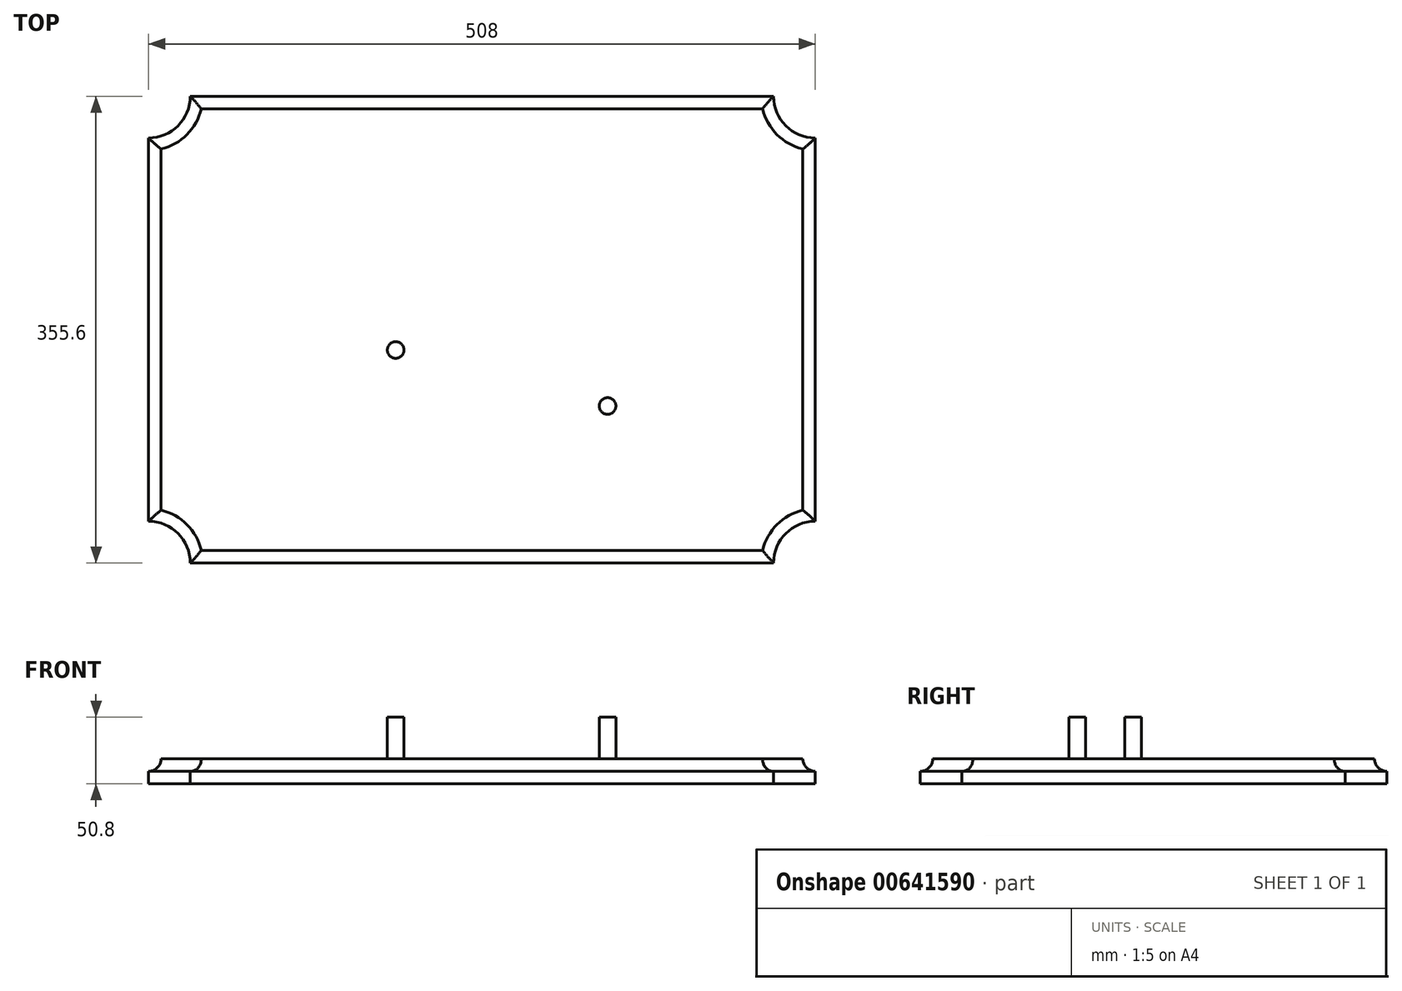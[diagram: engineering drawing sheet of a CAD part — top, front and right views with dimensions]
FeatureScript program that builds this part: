
annotation { "Feature Type Name" : "Feature", "Feature Type Description" : "" }
export const myFeature = defineFeature(function(context is Context, id is Id, definition is map)
    precondition{}
    {
        {
            var Q0;
            Q0=qCreatedBy(makeId("Top.planeOp"),FACE);
            var sketch = newSketch(context, id + "F0", { "sketchPlane" : qUnion([Q0])});
            skLineSegment(sketch, "E0.bottom", {"start": v(222.25, 177.8) * mm, "end": v(-222.25, 177.8) * mm});
            skLineSegment(sketch, "E0.top", {"start": v(222.25, -177.8) * mm, "end": v(-222.25, -177.8) * mm});
            skLineSegment(sketch, "E0.left", {"start": v(254, 146.05) * mm, "end": v(254, -146.05) * mm});
            skLineSegment(sketch, "E0.right", {"start": v(-254, 146.05) * mm, "end": v(-254, -146.05) * mm});
            skPoint(sketch, "E0.middle", {"position": v(0, 0) * mm});
            skArc(sketch, "E1", {"start": v(-254, 146.05) * mm, "mid": v(-231.55, 155.35) * mm, "end": v(-222.25, 177.8) * mm});
            skArc(sketch, "E2", {"start": v(-222.25, -177.8) * mm, "mid": v(-231.55, -155.35) * mm, "end": v(-254, -146.05) * mm});
            skArc(sketch, "E3", {"start": v(254, -146.05) * mm, "mid": v(231.55, -155.35) * mm, "end": v(222.25, -177.8) * mm});
            skArc(sketch, "E4", {"start": v(222.25, 177.8) * mm, "mid": v(231.55, 155.35) * mm, "end": v(254, 146.05) * mm});
            skSolve(sketch);
        }
        {
            var Q0;
            Q0=makeQuery(id+"F0.imprint","IMPRINT",FACE,{"disambiguationData":[TD([[makeQuery(id+"F0.imprint","IMPRINT",EDGE,{"derivedFrom":sQuery(id+"F0.wireOp",EDGE,"E0.bottom")}),1.0]])]});
            extrude(context, id + "F1", {"entities" : qUnion([Q0]), "depth" : 19.05 * mm, "offsetDistance" : 25.4 * mm});
        }
        {
            var Q0;
            Q0=qCreatedBy(makeId("Right.planeOp"),FACE);
            var sketch = newSketch(context, id + "F2", { "sketchPlane" : qUnion([Q0])});
            skLineSegment(sketch, "E5", {"start": v(-177.8, 0) * mm, "end": v(-177.8, 9.53) * mm});
            skLineSegment(sketch, "E6", {"start": v(-177.8, 0) * mm, "end": v(-180.98, 0) * mm});
            skLineSegment(sketch, "E7", {"start": v(-180.98, 0) * mm, "end": v(-180.98, 19.05) * mm});
            skLineSegment(sketch, "E8", {"start": v(-180.98, 19.05) * mm, "end": v(-168.28, 19.05) * mm});
            skArc(sketch, "E9", {"start": v(-177.8, 9.53) * mm, "mid": v(-171.06, 12.31) * mm, "end": v(-168.28, 19.05) * mm});
            skSolve(sketch);
        }
        {
            var Q0;
            Q0=makeQuery(id+"F2.imprint","IMPRINT",FACE,{"disambiguationData":[TD([[makeQuery(id+"F2.imprint","IMPRINT",EDGE,{"derivedFrom":sQuery(id+"F2.wireOp",EDGE,"E5")}),1.0]])]});
            var Q1;
            Q1 = qConstructionFilter(qBodyType(qCreatedBy(id + "F0" ,EDGE), BodyType.WIRE), ConstructionObject.NO);
            sweep(context, id + "F3", {"operationType" : NewBodyOperationType.REMOVE, "profiles" : qUnion([Q0]), "path" : qUnion([Q1])});
        }
        {
            var Q0;
            Q0=makeQuery(id+"F1.opExtrude","CAP_FACE",FACE,{"disambiguationData":[OSD([sQuery(id+"F0.wireOp",EDGE,"E0.bottom"),sQuery(id+"F0.wireOp",EDGE,"E0.top"),sQuery(id+"F0.wireOp",EDGE,"E0.left"),sQuery(id+"F0.wireOp",EDGE,"E0.right"),sQuery(id+"F0.wireOp",EDGE,"E1"),sQuery(id+"F0.wireOp",EDGE,"E2"),sQuery(id+"F0.wireOp",EDGE,"E3"),sQuery(id+"F0.wireOp",EDGE,"E4")])],"isStart":false});
            var sketch = newSketch(context, id + "F4", { "sketchPlane" : qUnion([Q0])});
            skLineSegment(sketch, "E10", {"start": v(-83.25, 0) * mm, "end": v(100.7, 0) * mm, "construction": true});
            skLineSegment(sketch, "E11.bottom", {"start": v(-129.39, 108.05) * mm, "end": v(150.01, 108.05) * mm, "construction": true});
            skLineSegment(sketch, "E11.top", {"start": v(-129.39, -106.43) * mm, "end": v(150.01, -106.43) * mm, "construction": true});
            skLineSegment(sketch, "E11.left", {"start": v(-129.39, 108.05) * mm, "end": v(-129.39, -106.43) * mm, "construction": true});
            skLineSegment(sketch, "E11.right", {"start": v(150.01, 108.05) * mm, "end": v(150.01, -106.43) * mm, "construction": true});
            skCircle(sketch, "E12", {"center": v(-65.72, -15.56) * mm, "radius": 6.35 * mm});
            skCircle(sketch, "E13", {"center": v(95.75, -58.2) * mm, "radius": 6.35 * mm});
            skSolve(sketch);
        }
        {
            var Q0;
            Q0 = qSketchRegion(id + "F4", true);
            extrude(context, id + "F5", {"entities" : qUnion([Q0]), "depth" : 31.75 * mm, "offsetDistance" : 25.4 * mm});
        }
    });
